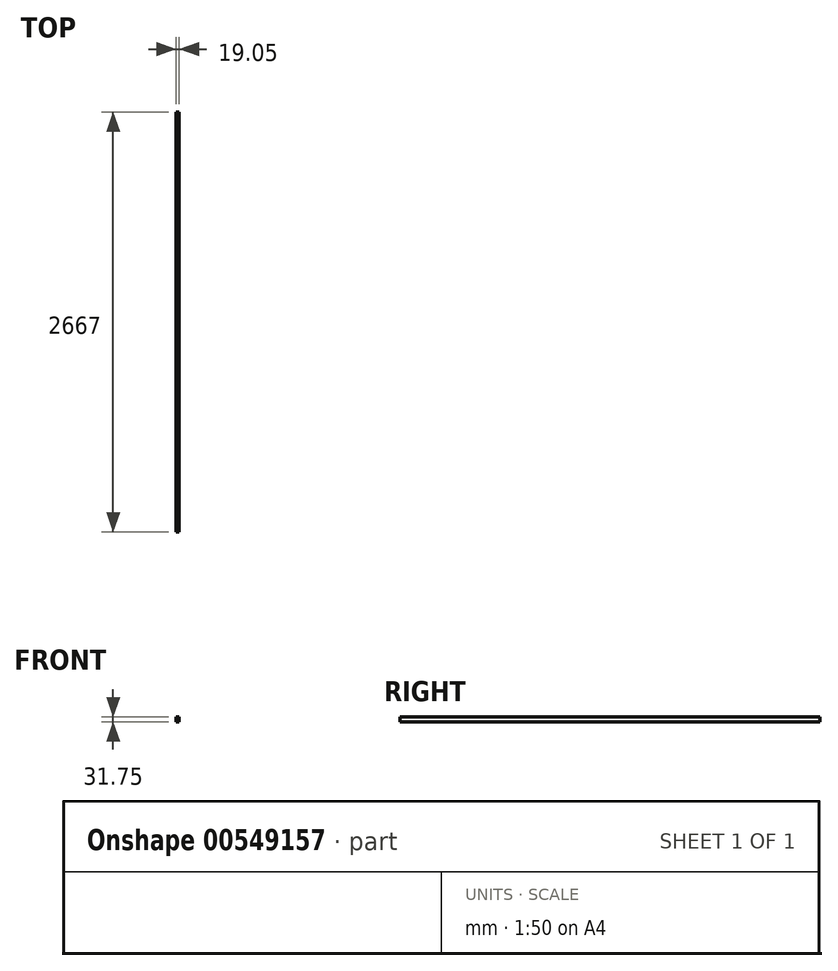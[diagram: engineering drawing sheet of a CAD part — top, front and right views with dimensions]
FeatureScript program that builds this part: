
annotation { "Feature Type Name" : "Feature", "Feature Type Description" : "" }
export const myFeature = defineFeature(function(context is Context, id is Id, definition is map)
    precondition{}
    {
        {
            var Q0;
            Q0=qCreatedBy(makeId("Front.planeOp"),FACE);
            var sketch = newSketch(context, id + "F0", { "sketchPlane" : qUnion([Q0])});
            skLineSegment(sketch, "E0", {"start": v(0, 0) * mm, "end": v(0, 31.75) * mm});
            skLineSegment(sketch, "E1", {"start": v(0, 31.75) * mm, "end": v(19.05, 31.75) * mm});
            skLineSegment(sketch, "E2", {"start": v(19.05, 31.75) * mm, "end": v(19.05, 0) * mm});
            skLineSegment(sketch, "E3", {"start": v(19.05, 0) * mm, "end": v(0, 0) * mm});
            skSolve(sketch);
        }
        {
            var Q0;
            Q0=makeQuery(id+"F0.imprint","IMPRINT",FACE,{"disambiguationData":[TD([[makeQuery(id+"F0.imprint","IMPRINT",EDGE,{"derivedFrom":sQuery(id+"F0.wireOp",EDGE,"E0")}),-1.0]])]});
            extrude(context, id + "F1", {"entities" : qUnion([Q0]), "depth" : 2667 * mm, "offsetDistance" : 25.4 * mm});
        }
    });
